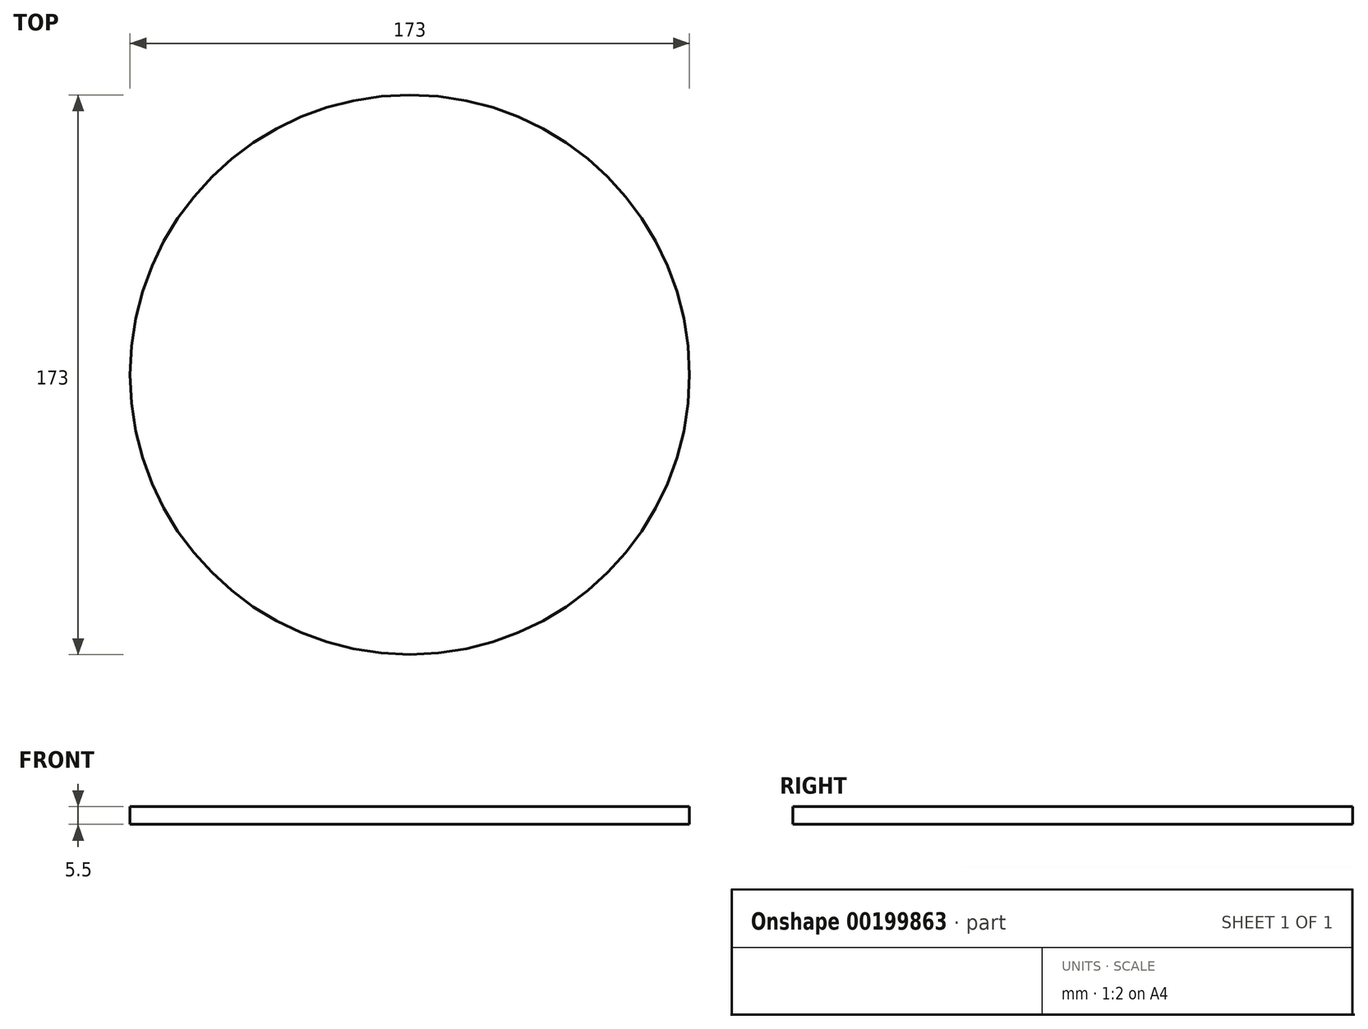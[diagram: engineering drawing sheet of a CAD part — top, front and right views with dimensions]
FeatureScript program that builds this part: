
annotation { "Feature Type Name" : "Feature", "Feature Type Description" : "" }
export const myFeature = defineFeature(function(context is Context, id is Id, definition is map)
    precondition{}
    {
        {
            var Q0;
            Q0=qCreatedBy(makeId("Top.planeOp"),FACE);
            var sketch = newSketch(context, id + "F0", { "sketchPlane" : qUnion([Q0])});
            skCircle(sketch, "E0", {"center": v(0, 0) * mm, "radius": 86.5 * mm});
            skLineSegment(sketch, "E1.bottom", {"start": v(29.9, 49.65) * mm, "end": v(-29.9, 49.65) * mm, "construction": true});
            skLineSegment(sketch, "E1.top", {"start": v(29.9, -49.65) * mm, "end": v(-29.9, -49.65) * mm, "construction": true});
            skLineSegment(sketch, "E1.left", {"start": v(29.9, 49.65) * mm, "end": v(29.9, -49.65) * mm, "construction": true});
            skLineSegment(sketch, "E1.right", {"start": v(-29.9, 49.65) * mm, "end": v(-29.9, -49.65) * mm, "construction": true});
            skCircle(sketch, "E2.cCircle", {"center": v(-29.9, 49.65) * mm, "radius": 2.9 * mm, "construction": true});
            skLineSegment(sketch, "E2.0", {"start": v(-31.57, 52.55) * mm, "end": v(-28.23, 52.55) * mm});
            skLineSegment(sketch, "E2.1", {"start": v(-28.23, 52.55) * mm, "end": v(-26.55, 49.65) * mm});
            skLineSegment(sketch, "E2.2", {"start": v(-26.55, 49.65) * mm, "end": v(-28.23, 46.75) * mm});
            skLineSegment(sketch, "E2.3", {"start": v(-28.23, 46.75) * mm, "end": v(-31.57, 46.75) * mm});
            skLineSegment(sketch, "E2.4", {"start": v(-31.57, 46.75) * mm, "end": v(-33.25, 49.65) * mm});
            skLineSegment(sketch, "E2.5", {"start": v(-33.25, 49.65) * mm, "end": v(-31.57, 52.55) * mm});
            skPoint(sketch, "E2.0.midPoint", {"position": v(-29.9, 52.55) * mm});
            skCircle(sketch, "E3.cCircle", {"center": v(29.9, 49.65) * mm, "radius": 2.9 * mm, "construction": true});
            skLineSegment(sketch, "E3.0", {"start": v(28.23, 52.55) * mm, "end": v(31.57, 52.55) * mm});
            skLineSegment(sketch, "E3.1", {"start": v(31.57, 52.55) * mm, "end": v(33.25, 49.65) * mm});
            skLineSegment(sketch, "E3.2", {"start": v(33.25, 49.65) * mm, "end": v(31.57, 46.75) * mm});
            skLineSegment(sketch, "E3.3", {"start": v(31.57, 46.75) * mm, "end": v(28.23, 46.75) * mm});
            skLineSegment(sketch, "E3.4", {"start": v(28.23, 46.75) * mm, "end": v(26.55, 49.65) * mm});
            skLineSegment(sketch, "E3.5", {"start": v(26.55, 49.65) * mm, "end": v(28.23, 52.55) * mm});
            skPoint(sketch, "E3.0.midPoint", {"position": v(29.9, 52.55) * mm});
            skCircle(sketch, "E4.cCircle", {"center": v(-29.9, -49.65) * mm, "radius": 2.9 * mm, "construction": true});
            skLineSegment(sketch, "E4.0", {"start": v(-28.23, -52.55) * mm, "end": v(-31.57, -52.55) * mm});
            skLineSegment(sketch, "E4.1", {"start": v(-31.57, -52.55) * mm, "end": v(-33.25, -49.65) * mm});
            skLineSegment(sketch, "E4.2", {"start": v(-33.25, -49.65) * mm, "end": v(-31.57, -46.75) * mm});
            skLineSegment(sketch, "E4.3", {"start": v(-31.57, -46.75) * mm, "end": v(-28.23, -46.75) * mm});
            skLineSegment(sketch, "E4.4", {"start": v(-28.23, -46.75) * mm, "end": v(-26.55, -49.65) * mm});
            skLineSegment(sketch, "E4.5", {"start": v(-26.55, -49.65) * mm, "end": v(-28.23, -52.55) * mm});
            skPoint(sketch, "E4.0.midPoint", {"position": v(-29.9, -52.55) * mm});
            skCircle(sketch, "E5.cCircle", {"center": v(29.9, -49.65) * mm, "radius": 2.9 * mm, "construction": true});
            skLineSegment(sketch, "E5.0", {"start": v(31.57, -52.55) * mm, "end": v(28.23, -52.55) * mm});
            skLineSegment(sketch, "E5.1", {"start": v(28.23, -52.55) * mm, "end": v(26.55, -49.65) * mm});
            skLineSegment(sketch, "E5.2", {"start": v(26.55, -49.65) * mm, "end": v(28.23, -46.75) * mm});
            skLineSegment(sketch, "E5.3", {"start": v(28.23, -46.75) * mm, "end": v(31.57, -46.75) * mm});
            skLineSegment(sketch, "E5.4", {"start": v(31.57, -46.75) * mm, "end": v(33.25, -49.65) * mm});
            skLineSegment(sketch, "E5.5", {"start": v(33.25, -49.65) * mm, "end": v(31.57, -52.55) * mm});
            skPoint(sketch, "E5.0.midPoint", {"position": v(29.9, -52.55) * mm});
            skLineSegment(sketch, "E6", {"start": v(0, 0) * mm, "end": v(125.93, 0) * mm, "construction": true});
            skCircle(sketch, "E7.0", {"center": v(0, 0) * mm, "radius": 85 * mm, "construction": true});
            skArc(sketch, "E8", {"start": v(84.99, 1.5) * mm, "mid": v(83.5, 0) * mm, "end": v(84.99, -1.5) * mm});
            skLineSegment(sketch, "E9.trimOffspring", {"start": v(84.97, 1.5) * mm, "end": v(86.49, 1.53) * mm});
            skLineSegment(sketch, "E10.trimOffspring", {"start": v(84.97, -1.5) * mm, "end": v(86.49, -1.53) * mm});
            skLineSegment(sketch, "E11.1.0", {"start": v(84.7, 6.89) * mm, "end": v(86.22, 7) * mm});
            skArc(sketch, "E11.1.1", {"start": v(84.72, 6.89) * mm, "mid": v(83.33, 5.3) * mm, "end": v(84.91, 3.9) * mm});
            skLineSegment(sketch, "E11.1.2", {"start": v(84.9, 3.9) * mm, "end": v(86.4, 3.96) * mm});
            skLineSegment(sketch, "E11.2.0", {"start": v(84.1, 12.24) * mm, "end": v(85.6, 12.46) * mm});
            skArc(sketch, "E11.2.1", {"start": v(84.11, 12.25) * mm, "mid": v(82.83, 10.57) * mm, "end": v(84.5, 9.27) * mm});
            skLineSegment(sketch, "E11.2.2", {"start": v(84.48, 9.27) * mm, "end": v(85.98, 9.43) * mm});
            skLineSegment(sketch, "E11.3.0", {"start": v(83.15, 17.55) * mm, "end": v(84.63, 17.87) * mm});
            skArc(sketch, "E11.3.1", {"start": v(83.17, 17.56) * mm, "mid": v(82, 15.8) * mm, "end": v(83.73, 14.61) * mm});
            skLineSegment(sketch, "E11.3.2", {"start": v(83.72, 14.6) * mm, "end": v(85.21, 14.87) * mm});
            skLineSegment(sketch, "E11.4.0", {"start": v(81.87, 22.8) * mm, "end": v(83.33, 23.2) * mm});
            skArc(sketch, "E11.4.1", {"start": v(81.89, 22.8) * mm, "mid": v(80.82, 20.97) * mm, "end": v(82.64, 19.9) * mm});
            skLineSegment(sketch, "E11.4.2", {"start": v(82.63, 19.89) * mm, "end": v(84.1, 20.24) * mm});
            skLineSegment(sketch, "E11.5.0", {"start": v(80.26, 27.94) * mm, "end": v(81.7, 28.44) * mm});
            skArc(sketch, "E11.5.1", {"start": v(80.28, 27.94) * mm, "mid": v(79.33, 26.05) * mm, "end": v(81.21, 25.1) * mm});
            skLineSegment(sketch, "E11.5.2", {"start": v(81.2, 25.09) * mm, "end": v(82.64, 25.54) * mm});
            skLineSegment(sketch, "E11.6.0", {"start": v(78.33, 32.97) * mm, "end": v(79.72, 33.56) * mm});
            skArc(sketch, "E11.6.1", {"start": v(78.34, 32.98) * mm, "mid": v(77.52, 31.03) * mm, "end": v(79.46, 30.2) * mm});
            skLineSegment(sketch, "E11.6.2", {"start": v(79.44, 30.19) * mm, "end": v(80.86, 30.73) * mm});
            skLineSegment(sketch, "E11.7.0", {"start": v(76.08, 37.88) * mm, "end": v(77.43, 38.55) * mm});
            skArc(sketch, "E11.7.1", {"start": v(76.1, 37.88) * mm, "mid": v(75.4, 35.89) * mm, "end": v(77.38, 35.17) * mm});
            skLineSegment(sketch, "E11.7.2", {"start": v(77.37, 35.17) * mm, "end": v(78.75, 35.8) * mm});
            skLineSegment(sketch, "E11.8.0", {"start": v(73.52, 42.62) * mm, "end": v(74.83, 43.38) * mm});
            skArc(sketch, "E11.8.1", {"start": v(73.54, 42.63) * mm, "mid": v(72.97, 40.6) * mm, "end": v(75, 40) * mm});
            skLineSegment(sketch, "E11.8.2", {"start": v(74.98, 40) * mm, "end": v(76.32, 40.72) * mm});
            skLineSegment(sketch, "E11.9.0", {"start": v(70.67, 47.2) * mm, "end": v(71.93, 48.04) * mm});
            skArc(sketch, "E11.9.1", {"start": v(70.68, 47.2) * mm, "mid": v(70.24, 45.14) * mm, "end": v(72.3, 44.69) * mm});
            skLineSegment(sketch, "E11.9.2", {"start": v(72.3, 44.68) * mm, "end": v(73.58, 45.47) * mm});
            skLineSegment(sketch, "E11.10.0", {"start": v(67.54, 51.59) * mm, "end": v(68.74, 52.5) * mm});
            skArc(sketch, "E11.10.1", {"start": v(67.55, 51.6) * mm, "mid": v(67.24, 49.5) * mm, "end": v(69.33, 49.18) * mm});
            skLineSegment(sketch, "E11.10.2", {"start": v(69.32, 49.17) * mm, "end": v(70.55, 50.05) * mm});
            skLineSegment(sketch, "E11.11.0", {"start": v(64.13, 55.77) * mm, "end": v(65.27, 56.76) * mm});
            skArc(sketch, "E11.11.1", {"start": v(64.14, 55.78) * mm, "mid": v(63.96, 53.67) * mm, "end": v(66.07, 53.48) * mm});
            skLineSegment(sketch, "E11.11.2", {"start": v(66.06, 53.47) * mm, "end": v(67.23, 54.42) * mm});
            skLineSegment(sketch, "E11.12.0", {"start": v(60.46, 59.72) * mm, "end": v(61.54, 60.79) * mm});
            skArc(sketch, "E11.12.1", {"start": v(60.47, 59.73) * mm, "mid": v(60.43, 57.62) * mm, "end": v(62.54, 57.56) * mm});
            skLineSegment(sketch, "E11.12.2", {"start": v(62.53, 57.55) * mm, "end": v(63.65, 58.58) * mm});
            skLineSegment(sketch, "E11.13.0", {"start": v(56.55, 63.44) * mm, "end": v(57.56, 64.57) * mm});
            skArc(sketch, "E11.13.1", {"start": v(56.56, 63.45) * mm, "mid": v(56.66, 61.34) * mm, "end": v(58.77, 61.41) * mm});
            skLineSegment(sketch, "E11.13.2", {"start": v(58.76, 61.4) * mm, "end": v(59.8, 62.5) * mm});
            skLineSegment(sketch, "E11.14.0", {"start": v(52.42, 66.9) * mm, "end": v(53.35, 68.09) * mm});
            skArc(sketch, "E11.14.1", {"start": v(52.42, 66.9) * mm, "mid": v(52.65, 64.8) * mm, "end": v(54.75, 65.02) * mm});
            skLineSegment(sketch, "E11.14.2", {"start": v(54.74, 65) * mm, "end": v(55.72, 66.16) * mm});
            skLineSegment(sketch, "E11.15.0", {"start": v(48.07, 70.09) * mm, "end": v(48.92, 71.34) * mm});
            skArc(sketch, "E11.15.1", {"start": v(48.08, 70.1) * mm, "mid": v(48.43, 68.02) * mm, "end": v(50.52, 68.36) * mm});
            skLineSegment(sketch, "E11.15.2", {"start": v(50.51, 68.35) * mm, "end": v(51.41, 69.56) * mm});
            skLineSegment(sketch, "E11.16.0", {"start": v(43.53, 73) * mm, "end": v(44.3, 74.3) * mm});
            skArc(sketch, "E11.16.1", {"start": v(43.53, 73) * mm, "mid": v(44.02, 70.95) * mm, "end": v(46.08, 71.42) * mm});
            skLineSegment(sketch, "E11.16.2", {"start": v(46.07, 71.41) * mm, "end": v(46.9, 72.69) * mm});
            skLineSegment(sketch, "E11.17.0", {"start": v(38.8, 75.6) * mm, "end": v(39.5, 76.95) * mm});
            skArc(sketch, "E11.17.1", {"start": v(38.81, 75.62) * mm, "mid": v(39.43, 73.6) * mm, "end": v(41.46, 74.2) * mm});
            skLineSegment(sketch, "E11.17.2", {"start": v(41.45, 74.2) * mm, "end": v(42.2, 75.51) * mm});
            skLineSegment(sketch, "E11.18.0", {"start": v(33.94, 77.92) * mm, "end": v(34.54, 79.3) * mm});
            skArc(sketch, "E11.18.1", {"start": v(33.94, 77.93) * mm, "mid": v(34.69, 75.95) * mm, "end": v(36.67, 76.68) * mm});
            skLineSegment(sketch, "E11.18.2", {"start": v(36.66, 76.67) * mm, "end": v(37.32, 78.04) * mm});
            skLineSegment(sketch, "E11.19.0", {"start": v(28.92, 79.91) * mm, "end": v(29.44, 81.34) * mm});
            skArc(sketch, "E11.19.1", {"start": v(28.93, 79.93) * mm, "mid": v(29.8, 78) * mm, "end": v(31.73, 78.85) * mm});
            skLineSegment(sketch, "E11.19.2", {"start": v(31.73, 78.84) * mm, "end": v(32.3, 80.25) * mm});
            skLineSegment(sketch, "E11.20.0", {"start": v(23.8, 81.59) * mm, "end": v(24.22, 83.04) * mm});
            skArc(sketch, "E11.20.1", {"start": v(23.8, 81.6) * mm, "mid": v(24.8, 79.73) * mm, "end": v(26.67, 80.7) * mm});
            skLineSegment(sketch, "E11.20.2", {"start": v(26.66, 80.7) * mm, "end": v(27.14, 82.13) * mm});
            skLineSegment(sketch, "E11.21.0", {"start": v(18.58, 82.93) * mm, "end": v(18.9, 84.4) * mm});
            skArc(sketch, "E11.21.1", {"start": v(18.58, 82.94) * mm, "mid": v(19.69, 81.15) * mm, "end": v(21.5, 82.24) * mm});
            skLineSegment(sketch, "E11.21.2", {"start": v(21.5, 82.22) * mm, "end": v(21.87, 83.69) * mm});
            skLineSegment(sketch, "E11.22.0", {"start": v(13.28, 83.94) * mm, "end": v(13.51, 85.44) * mm});
            skArc(sketch, "E11.22.1", {"start": v(13.28, 83.96) * mm, "mid": v(14.5, 82.23) * mm, "end": v(16.23, 83.44) * mm});
            skLineSegment(sketch, "E11.22.2", {"start": v(16.23, 83.42) * mm, "end": v(16.52, 84.9) * mm});
            skLineSegment(sketch, "E11.23.0", {"start": v(7.93, 84.62) * mm, "end": v(8.07, 86.12) * mm});
            skArc(sketch, "E11.23.1", {"start": v(7.93, 84.63) * mm, "mid": v(9.25, 82.99) * mm, "end": v(10.91, 84.3) * mm});
            skLineSegment(sketch, "E11.23.2", {"start": v(10.9, 84.28) * mm, "end": v(11.1, 85.78) * mm});
            skLineSegment(sketch, "E11.24.0", {"start": v(2.55, 84.95) * mm, "end": v(2.6, 86.46) * mm});
            skArc(sketch, "E11.24.1", {"start": v(2.55, 84.96) * mm, "mid": v(3.97, 83.4) * mm, "end": v(5.54, 84.82) * mm});
            skLineSegment(sketch, "E11.24.2", {"start": v(5.54, 84.8) * mm, "end": v(5.64, 86.32) * mm});
            skLineSegment(sketch, "E11.25.0", {"start": v(-2.85, 84.94) * mm, "end": v(-2.9, 86.45) * mm});
            skArc(sketch, "E11.25.1", {"start": v(-2.85, 84.95) * mm, "mid": v(-1.32, 83.49) * mm, "end": v(0.15, 85) * mm});
            skLineSegment(sketch, "E11.25.2", {"start": v(0.15, 84.99) * mm, "end": v(0.15, 86.5) * mm});
            skLineSegment(sketch, "E11.26.0", {"start": v(-8.23, 84.59) * mm, "end": v(-8.38, 86.1) * mm});
            skArc(sketch, "E11.26.1", {"start": v(-8.23, 84.6) * mm, "mid": v(-6.62, 83.24) * mm, "end": v(-5.24, 84.84) * mm});
            skLineSegment(sketch, "E11.26.2", {"start": v(-5.24, 84.83) * mm, "end": v(-5.33, 86.34) * mm});
            skLineSegment(sketch, "E11.27.0", {"start": v(-13.58, 83.9) * mm, "end": v(-13.82, 85.39) * mm});
            skArc(sketch, "E11.27.1", {"start": v(-13.58, 83.9) * mm, "mid": v(-11.88, 82.65) * mm, "end": v(-10.61, 84.34) * mm});
            skLineSegment(sketch, "E11.27.2", {"start": v(-10.6, 84.32) * mm, "end": v(-10.8, 85.82) * mm});
            skLineSegment(sketch, "E11.28.0", {"start": v(-18.87, 82.87) * mm, "end": v(-19.2, 84.34) * mm});
            skArc(sketch, "E11.28.1", {"start": v(-18.87, 82.88) * mm, "mid": v(-17.1, 81.73) * mm, "end": v(-15.94, 83.5) * mm});
            skLineSegment(sketch, "E11.28.2", {"start": v(-15.94, 83.48) * mm, "end": v(-16.22, 84.97) * mm});
            skLineSegment(sketch, "E11.29.0", {"start": v(-24.09, 81.5) * mm, "end": v(-24.52, 82.95) * mm});
            skArc(sketch, "E11.29.1", {"start": v(-24.1, 81.51) * mm, "mid": v(-22.25, 80.48) * mm, "end": v(-21.2, 82.31) * mm});
            skLineSegment(sketch, "E11.29.2", {"start": v(-21.2, 82.3) * mm, "end": v(-21.58, 83.77) * mm});
            skLineSegment(sketch, "E11.30.0", {"start": v(-29.2, 79.8) * mm, "end": v(-29.73, 81.23) * mm});
            skArc(sketch, "E11.30.1", {"start": v(-29.21, 79.82) * mm, "mid": v(-27.31, 78.9) * mm, "end": v(-26.38, 80.8) * mm});
            skLineSegment(sketch, "E11.30.2", {"start": v(-26.37, 80.8) * mm, "end": v(-26.84, 82.23) * mm});
            skLineSegment(sketch, "E11.31.0", {"start": v(-34.21, 77.8) * mm, "end": v(-34.82, 79.18) * mm});
            skArc(sketch, "E11.31.1", {"start": v(-34.22, 77.8) * mm, "mid": v(-32.26, 77.02) * mm, "end": v(-31.45, 78.97) * mm});
            skLineSegment(sketch, "E11.31.2", {"start": v(-31.45, 78.96) * mm, "end": v(-32, 80.36) * mm});
            skLineSegment(sketch, "E11.32.0", {"start": v(-39.08, 75.47) * mm, "end": v(-39.77, 76.81) * mm});
            skArc(sketch, "E11.32.1", {"start": v(-39.08, 75.48) * mm, "mid": v(-37.08, 74.82) * mm, "end": v(-36.4, 76.81) * mm});
            skLineSegment(sketch, "E11.32.2", {"start": v(-36.4, 76.8) * mm, "end": v(-37.04, 78.17) * mm});
            skLineSegment(sketch, "E11.33.0", {"start": v(-43.79, 72.84) * mm, "end": v(-44.57, 74.14) * mm});
            skArc(sketch, "E11.33.1", {"start": v(-43.8, 72.85) * mm, "mid": v(-41.75, 72.31) * mm, "end": v(-41.2, 74.35) * mm});
            skLineSegment(sketch, "E11.33.2", {"start": v(-41.19, 74.34) * mm, "end": v(-41.92, 75.66) * mm});
            skLineSegment(sketch, "E11.34.0", {"start": v(-48.32, 69.92) * mm, "end": v(-49.18, 71.16) * mm});
            skArc(sketch, "E11.34.1", {"start": v(-48.32, 69.93) * mm, "mid": v(-46.25, 69.52) * mm, "end": v(-45.83, 71.59) * mm});
            skLineSegment(sketch, "E11.34.2", {"start": v(-45.82, 71.58) * mm, "end": v(-46.64, 72.85) * mm});
            skLineSegment(sketch, "E11.35.0", {"start": v(-52.65, 66.71) * mm, "end": v(-53.6, 67.9) * mm});
            skArc(sketch, "E11.35.1", {"start": v(-52.66, 66.72) * mm, "mid": v(-50.57, 66.45) * mm, "end": v(-50.28, 68.54) * mm});
            skLineSegment(sketch, "E11.35.2", {"start": v(-50.27, 68.53) * mm, "end": v(-51.16, 69.75) * mm});
            skLineSegment(sketch, "E11.36.0", {"start": v(-56.78, 63.24) * mm, "end": v(-57.8, 64.36) * mm});
            skArc(sketch, "E11.36.1", {"start": v(-56.79, 63.25) * mm, "mid": v(-54.68, 63.1) * mm, "end": v(-54.52, 65.21) * mm});
            skLineSegment(sketch, "E11.36.2", {"start": v(-54.51, 65.2) * mm, "end": v(-55.48, 66.36) * mm});
            skLineSegment(sketch, "E11.37.0", {"start": v(-60.68, 59.5) * mm, "end": v(-61.76, 60.57) * mm});
            skArc(sketch, "E11.37.1", {"start": v(-60.69, 59.52) * mm, "mid": v(-58.57, 59.5) * mm, "end": v(-58.55, 61.62) * mm});
            skLineSegment(sketch, "E11.37.2", {"start": v(-58.54, 61.61) * mm, "end": v(-59.58, 62.7) * mm});
            skLineSegment(sketch, "E11.38.0", {"start": v(-64.33, 55.54) * mm, "end": v(-65.47, 56.53) * mm});
            skArc(sketch, "E11.38.1", {"start": v(-64.34, 55.55) * mm, "mid": v(-62.23, 55.68) * mm, "end": v(-62.34, 57.78) * mm});
            skLineSegment(sketch, "E11.38.2", {"start": v(-62.33, 57.78) * mm, "end": v(-63.44, 58.8) * mm});
            skLineSegment(sketch, "E11.39.0", {"start": v(-67.72, 51.35) * mm, "end": v(-68.93, 52.26) * mm});
            skArc(sketch, "E11.39.1", {"start": v(-67.73, 51.36) * mm, "mid": v(-65.64, 51.62) * mm, "end": v(-65.88, 53.71) * mm});
            skLineSegment(sketch, "E11.39.2", {"start": v(-65.87, 53.7) * mm, "end": v(-67.04, 54.66) * mm});
            skLineSegment(sketch, "E11.40.0", {"start": v(-70.84, 46.95) * mm, "end": v(-72.1, 47.79) * mm});
            skArc(sketch, "E11.40.1", {"start": v(-70.85, 46.96) * mm, "mid": v(-68.78, 47.35) * mm, "end": v(-69.15, 49.43) * mm});
            skLineSegment(sketch, "E11.40.2", {"start": v(-69.14, 49.42) * mm, "end": v(-70.37, 50.3) * mm});
            skLineSegment(sketch, "E11.41.0", {"start": v(-73.68, 42.36) * mm, "end": v(-74.99, 43.12) * mm});
            skArc(sketch, "E11.41.1", {"start": v(-73.69, 42.37) * mm, "mid": v(-71.64, 42.9) * mm, "end": v(-72.15, 44.94) * mm});
            skLineSegment(sketch, "E11.41.2", {"start": v(-72.14, 44.94) * mm, "end": v(-73.42, 45.74) * mm});
            skLineSegment(sketch, "E11.42.0", {"start": v(-76.21, 37.6) * mm, "end": v(-77.57, 38.27) * mm});
            skArc(sketch, "E11.42.1", {"start": v(-76.23, 37.6) * mm, "mid": v(-74.22, 38.26) * mm, "end": v(-74.85, 40.28) * mm});
            skLineSegment(sketch, "E11.42.2", {"start": v(-74.84, 40.27) * mm, "end": v(-76.17, 40.99) * mm});
            skLineSegment(sketch, "E11.43.0", {"start": v(-78.45, 32.7) * mm, "end": v(-79.84, 33.28) * mm});
            skArc(sketch, "E11.43.1", {"start": v(-78.46, 32.7) * mm, "mid": v(-76.5, 33.48) * mm, "end": v(-77.26, 35.45) * mm});
            skLineSegment(sketch, "E11.43.2", {"start": v(-77.24, 35.44) * mm, "end": v(-78.62, 36.07) * mm});
            skLineSegment(sketch, "E11.44.0", {"start": v(-80.36, 27.65) * mm, "end": v(-81.8, 28.15) * mm});
            skArc(sketch, "E11.44.1", {"start": v(-80.37, 27.66) * mm, "mid": v(-78.46, 28.56) * mm, "end": v(-79.35, 30.48) * mm});
            skLineSegment(sketch, "E11.44.2", {"start": v(-79.34, 30.47) * mm, "end": v(-80.75, 31.01) * mm});
            skLineSegment(sketch, "E11.45.0", {"start": v(-81.95, 22.5) * mm, "end": v(-83.41, 22.9) * mm});
            skArc(sketch, "E11.45.1", {"start": v(-81.97, 22.5) * mm, "mid": v(-80.12, 23.52) * mm, "end": v(-81.12, 25.38) * mm});
            skLineSegment(sketch, "E11.45.2", {"start": v(-81.1, 25.38) * mm, "end": v(-82.55, 25.83) * mm});
            skLineSegment(sketch, "E11.46.0", {"start": v(-83.22, 17.26) * mm, "end": v(-84.7, 17.56) * mm});
            skArc(sketch, "E11.46.1", {"start": v(-83.23, 17.26) * mm, "mid": v(-81.45, 18.4) * mm, "end": v(-82.57, 20.19) * mm});
            skLineSegment(sketch, "E11.46.2", {"start": v(-82.56, 20.18) * mm, "end": v(-84.03, 20.54) * mm});
            skLineSegment(sketch, "E11.47.0", {"start": v(-84.14, 11.95) * mm, "end": v(-85.64, 12.16) * mm});
            skArc(sketch, "E11.47.1", {"start": v(-84.16, 11.95) * mm, "mid": v(-82.45, 13.2) * mm, "end": v(-83.68, 14.9) * mm});
            skLineSegment(sketch, "E11.47.2", {"start": v(-83.67, 14.9) * mm, "end": v(-85.16, 15.17) * mm});
            skLineSegment(sketch, "E11.48.0", {"start": v(-84.73, 6.58) * mm, "end": v(-86.24, 6.7) * mm});
            skArc(sketch, "E11.48.1", {"start": v(-84.74, 6.59) * mm, "mid": v(-83.12, 7.94) * mm, "end": v(-84.46, 9.57) * mm});
            skLineSegment(sketch, "E11.48.2", {"start": v(-84.45, 9.57) * mm, "end": v(-85.95, 9.74) * mm});
            skLineSegment(sketch, "E11.49.0", {"start": v(-84.98, 1.2) * mm, "end": v(-86.5, 1.22) * mm});
            skArc(sketch, "E11.49.1", {"start": v(-85, 1.2) * mm, "mid": v(-83.46, 2.65) * mm, "end": v(-84.9, 4.2) * mm});
            skLineSegment(sketch, "E11.49.2", {"start": v(-84.88, 4.2) * mm, "end": v(-86.4, 4.27) * mm});
            skLineSegment(sketch, "E11.50.0", {"start": v(-84.88, -4.2) * mm, "end": v(-86.4, -4.27) * mm});
            skArc(sketch, "E11.50.1", {"start": v(-84.9, -4.2) * mm, "mid": v(-83.46, -2.65) * mm, "end": v(-85, -1.2) * mm});
            skLineSegment(sketch, "E11.50.2", {"start": v(-84.98, -1.2) * mm, "end": v(-86.5, -1.22) * mm});
            skLineSegment(sketch, "E11.51.0", {"start": v(-84.45, -9.57) * mm, "end": v(-85.95, -9.74) * mm});
            skArc(sketch, "E11.51.1", {"start": v(-84.46, -9.57) * mm, "mid": v(-83.12, -7.94) * mm, "end": v(-84.74, -6.59) * mm});
            skLineSegment(sketch, "E11.51.2", {"start": v(-84.73, -6.58) * mm, "end": v(-86.24, -6.7) * mm});
            skLineSegment(sketch, "E11.52.0", {"start": v(-83.67, -14.9) * mm, "end": v(-85.16, -15.17) * mm});
            skArc(sketch, "E11.52.1", {"start": v(-83.68, -14.9) * mm, "mid": v(-82.45, -13.2) * mm, "end": v(-84.16, -11.95) * mm});
            skLineSegment(sketch, "E11.52.2", {"start": v(-84.14, -11.95) * mm, "end": v(-85.64, -12.16) * mm});
            skLineSegment(sketch, "E11.53.0", {"start": v(-82.56, -20.18) * mm, "end": v(-84.03, -20.54) * mm});
            skArc(sketch, "E11.53.1", {"start": v(-82.57, -20.19) * mm, "mid": v(-81.45, -18.4) * mm, "end": v(-83.23, -17.26) * mm});
            skLineSegment(sketch, "E11.53.2", {"start": v(-83.22, -17.26) * mm, "end": v(-84.7, -17.56) * mm});
            skLineSegment(sketch, "E11.54.0", {"start": v(-81.1, -25.38) * mm, "end": v(-82.55, -25.83) * mm});
            skArc(sketch, "E11.54.1", {"start": v(-81.12, -25.38) * mm, "mid": v(-80.12, -23.52) * mm, "end": v(-81.97, -22.5) * mm});
            skLineSegment(sketch, "E11.54.2", {"start": v(-81.95, -22.5) * mm, "end": v(-83.41, -22.9) * mm});
            skLineSegment(sketch, "E11.55.0", {"start": v(-79.34, -30.47) * mm, "end": v(-80.75, -31.01) * mm});
            skArc(sketch, "E11.55.1", {"start": v(-79.35, -30.48) * mm, "mid": v(-78.46, -28.56) * mm, "end": v(-80.37, -27.66) * mm});
            skLineSegment(sketch, "E11.55.2", {"start": v(-80.36, -27.65) * mm, "end": v(-81.8, -28.15) * mm});
            skLineSegment(sketch, "E11.56.0", {"start": v(-77.24, -35.44) * mm, "end": v(-78.62, -36.07) * mm});
            skArc(sketch, "E11.56.1", {"start": v(-77.26, -35.45) * mm, "mid": v(-76.5, -33.48) * mm, "end": v(-78.46, -32.7) * mm});
            skLineSegment(sketch, "E11.56.2", {"start": v(-78.45, -32.7) * mm, "end": v(-79.84, -33.28) * mm});
            skLineSegment(sketch, "E11.57.0", {"start": v(-74.84, -40.27) * mm, "end": v(-76.17, -40.99) * mm});
            skArc(sketch, "E11.57.1", {"start": v(-74.85, -40.28) * mm, "mid": v(-74.22, -38.26) * mm, "end": v(-76.23, -37.6) * mm});
            skLineSegment(sketch, "E11.57.2", {"start": v(-76.21, -37.6) * mm, "end": v(-77.57, -38.27) * mm});
            skLineSegment(sketch, "E11.58.0", {"start": v(-72.14, -44.94) * mm, "end": v(-73.42, -45.74) * mm});
            skArc(sketch, "E11.58.1", {"start": v(-72.15, -44.94) * mm, "mid": v(-71.64, -42.9) * mm, "end": v(-73.69, -42.37) * mm});
            skLineSegment(sketch, "E11.58.2", {"start": v(-73.68, -42.36) * mm, "end": v(-74.99, -43.12) * mm});
            skLineSegment(sketch, "E11.59.0", {"start": v(-69.14, -49.42) * mm, "end": v(-70.37, -50.3) * mm});
            skArc(sketch, "E11.59.1", {"start": v(-69.15, -49.43) * mm, "mid": v(-68.78, -47.35) * mm, "end": v(-70.85, -46.96) * mm});
            skLineSegment(sketch, "E11.59.2", {"start": v(-70.84, -46.95) * mm, "end": v(-72.1, -47.79) * mm});
            skLineSegment(sketch, "E11.60.0", {"start": v(-65.87, -53.7) * mm, "end": v(-67.04, -54.66) * mm});
            skArc(sketch, "E11.60.1", {"start": v(-65.88, -53.71) * mm, "mid": v(-65.64, -51.62) * mm, "end": v(-67.73, -51.36) * mm});
            skLineSegment(sketch, "E11.60.2", {"start": v(-67.72, -51.35) * mm, "end": v(-68.93, -52.26) * mm});
            skLineSegment(sketch, "E11.61.0", {"start": v(-62.33, -57.78) * mm, "end": v(-63.44, -58.8) * mm});
            skArc(sketch, "E11.61.1", {"start": v(-62.34, -57.78) * mm, "mid": v(-62.23, -55.68) * mm, "end": v(-64.34, -55.55) * mm});
            skLineSegment(sketch, "E11.61.2", {"start": v(-64.33, -55.54) * mm, "end": v(-65.47, -56.53) * mm});
            skLineSegment(sketch, "E11.62.0", {"start": v(-58.54, -61.61) * mm, "end": v(-59.58, -62.7) * mm});
            skArc(sketch, "E11.62.1", {"start": v(-58.55, -61.62) * mm, "mid": v(-58.57, -59.5) * mm, "end": v(-60.69, -59.52) * mm});
            skLineSegment(sketch, "E11.62.2", {"start": v(-60.68, -59.5) * mm, "end": v(-61.76, -60.57) * mm});
            skLineSegment(sketch, "E11.63.0", {"start": v(-54.51, -65.2) * mm, "end": v(-55.48, -66.36) * mm});
            skArc(sketch, "E11.63.1", {"start": v(-54.52, -65.21) * mm, "mid": v(-54.68, -63.1) * mm, "end": v(-56.79, -63.25) * mm});
            skLineSegment(sketch, "E11.63.2", {"start": v(-56.78, -63.24) * mm, "end": v(-57.8, -64.36) * mm});
            skLineSegment(sketch, "E11.64.0", {"start": v(-50.27, -68.53) * mm, "end": v(-51.16, -69.75) * mm});
            skArc(sketch, "E11.64.1", {"start": v(-50.28, -68.54) * mm, "mid": v(-50.57, -66.45) * mm, "end": v(-52.66, -66.72) * mm});
            skLineSegment(sketch, "E11.64.2", {"start": v(-52.65, -66.71) * mm, "end": v(-53.6, -67.9) * mm});
            skLineSegment(sketch, "E11.65.0", {"start": v(-45.82, -71.58) * mm, "end": v(-46.64, -72.85) * mm});
            skArc(sketch, "E11.65.1", {"start": v(-45.83, -71.59) * mm, "mid": v(-46.25, -69.52) * mm, "end": v(-48.32, -69.93) * mm});
            skLineSegment(sketch, "E11.65.2", {"start": v(-48.32, -69.92) * mm, "end": v(-49.18, -71.16) * mm});
            skLineSegment(sketch, "E11.66.0", {"start": v(-41.19, -74.34) * mm, "end": v(-41.92, -75.66) * mm});
            skArc(sketch, "E11.66.1", {"start": v(-41.2, -74.35) * mm, "mid": v(-41.75, -72.31) * mm, "end": v(-43.8, -72.85) * mm});
            skLineSegment(sketch, "E11.66.2", {"start": v(-43.79, -72.84) * mm, "end": v(-44.57, -74.14) * mm});
            skLineSegment(sketch, "E11.67.0", {"start": v(-36.4, -76.8) * mm, "end": v(-37.04, -78.17) * mm});
            skArc(sketch, "E11.67.1", {"start": v(-36.4, -76.81) * mm, "mid": v(-37.08, -74.82) * mm, "end": v(-39.08, -75.48) * mm});
            skLineSegment(sketch, "E11.67.2", {"start": v(-39.08, -75.47) * mm, "end": v(-39.77, -76.81) * mm});
            skLineSegment(sketch, "E11.68.0", {"start": v(-31.45, -78.96) * mm, "end": v(-32, -80.36) * mm});
            skArc(sketch, "E11.68.1", {"start": v(-31.45, -78.97) * mm, "mid": v(-32.26, -77.02) * mm, "end": v(-34.22, -77.8) * mm});
            skLineSegment(sketch, "E11.68.2", {"start": v(-34.21, -77.8) * mm, "end": v(-34.82, -79.18) * mm});
            skLineSegment(sketch, "E11.69.0", {"start": v(-26.37, -80.8) * mm, "end": v(-26.84, -82.23) * mm});
            skArc(sketch, "E11.69.1", {"start": v(-26.38, -80.8) * mm, "mid": v(-27.31, -78.9) * mm, "end": v(-29.21, -79.82) * mm});
            skLineSegment(sketch, "E11.69.2", {"start": v(-29.2, -79.8) * mm, "end": v(-29.73, -81.23) * mm});
            skLineSegment(sketch, "E11.70.0", {"start": v(-21.2, -82.3) * mm, "end": v(-21.58, -83.77) * mm});
            skArc(sketch, "E11.70.1", {"start": v(-21.2, -82.31) * mm, "mid": v(-22.25, -80.48) * mm, "end": v(-24.1, -81.51) * mm});
            skLineSegment(sketch, "E11.70.2", {"start": v(-24.09, -81.5) * mm, "end": v(-24.52, -82.95) * mm});
            skLineSegment(sketch, "E11.71.0", {"start": v(-15.94, -83.48) * mm, "end": v(-16.22, -84.97) * mm});
            skArc(sketch, "E11.71.1", {"start": v(-15.94, -83.5) * mm, "mid": v(-17.1, -81.73) * mm, "end": v(-18.87, -82.88) * mm});
            skLineSegment(sketch, "E11.71.2", {"start": v(-18.87, -82.87) * mm, "end": v(-19.2, -84.34) * mm});
            skLineSegment(sketch, "E11.72.0", {"start": v(-10.6, -84.32) * mm, "end": v(-10.8, -85.82) * mm});
            skArc(sketch, "E11.72.1", {"start": v(-10.61, -84.34) * mm, "mid": v(-11.88, -82.65) * mm, "end": v(-13.58, -83.9) * mm});
            skLineSegment(sketch, "E11.72.2", {"start": v(-13.58, -83.9) * mm, "end": v(-13.82, -85.39) * mm});
            skLineSegment(sketch, "E11.73.0", {"start": v(-5.24, -84.83) * mm, "end": v(-5.33, -86.34) * mm});
            skArc(sketch, "E11.73.1", {"start": v(-5.24, -84.84) * mm, "mid": v(-6.62, -83.24) * mm, "end": v(-8.23, -84.6) * mm});
            skLineSegment(sketch, "E11.73.2", {"start": v(-8.23, -84.59) * mm, "end": v(-8.38, -86.1) * mm});
            skLineSegment(sketch, "E11.74.0", {"start": v(0.15, -84.99) * mm, "end": v(0.15, -86.5) * mm});
            skArc(sketch, "E11.74.1", {"start": v(0.15, -85) * mm, "mid": v(-1.32, -83.49) * mm, "end": v(-2.85, -84.95) * mm});
            skLineSegment(sketch, "E11.74.2", {"start": v(-2.85, -84.94) * mm, "end": v(-2.9, -86.45) * mm});
            skLineSegment(sketch, "E11.75.0", {"start": v(5.54, -84.8) * mm, "end": v(5.64, -86.32) * mm});
            skArc(sketch, "E11.75.1", {"start": v(5.54, -84.82) * mm, "mid": v(3.97, -83.4) * mm, "end": v(2.55, -84.96) * mm});
            skLineSegment(sketch, "E11.75.2", {"start": v(2.55, -84.95) * mm, "end": v(2.6, -86.46) * mm});
            skLineSegment(sketch, "E11.76.0", {"start": v(10.9, -84.28) * mm, "end": v(11.1, -85.78) * mm});
            skArc(sketch, "E11.76.1", {"start": v(10.91, -84.3) * mm, "mid": v(9.25, -82.99) * mm, "end": v(7.93, -84.63) * mm});
            skLineSegment(sketch, "E11.76.2", {"start": v(7.93, -84.62) * mm, "end": v(8.07, -86.12) * mm});
            skLineSegment(sketch, "E11.77.0", {"start": v(16.23, -83.42) * mm, "end": v(16.52, -84.9) * mm});
            skArc(sketch, "E11.77.1", {"start": v(16.23, -83.44) * mm, "mid": v(14.5, -82.23) * mm, "end": v(13.28, -83.96) * mm});
            skLineSegment(sketch, "E11.77.2", {"start": v(13.28, -83.94) * mm, "end": v(13.51, -85.44) * mm});
            skLineSegment(sketch, "E11.78.0", {"start": v(21.5, -82.22) * mm, "end": v(21.87, -83.69) * mm});
            skArc(sketch, "E11.78.1", {"start": v(21.5, -82.24) * mm, "mid": v(19.69, -81.15) * mm, "end": v(18.58, -82.94) * mm});
            skLineSegment(sketch, "E11.78.2", {"start": v(18.58, -82.93) * mm, "end": v(18.9, -84.4) * mm});
            skLineSegment(sketch, "E11.79.0", {"start": v(26.66, -80.7) * mm, "end": v(27.14, -82.13) * mm});
            skArc(sketch, "E11.79.1", {"start": v(26.67, -80.7) * mm, "mid": v(24.8, -79.73) * mm, "end": v(23.8, -81.6) * mm});
            skLineSegment(sketch, "E11.79.2", {"start": v(23.8, -81.59) * mm, "end": v(24.22, -83.04) * mm});
            skLineSegment(sketch, "E11.80.0", {"start": v(31.73, -78.84) * mm, "end": v(32.3, -80.25) * mm});
            skArc(sketch, "E11.80.1", {"start": v(31.73, -78.85) * mm, "mid": v(29.8, -78) * mm, "end": v(28.93, -79.93) * mm});
            skLineSegment(sketch, "E11.80.2", {"start": v(28.92, -79.91) * mm, "end": v(29.44, -81.34) * mm});
            skLineSegment(sketch, "E11.81.0", {"start": v(36.66, -76.67) * mm, "end": v(37.32, -78.04) * mm});
            skArc(sketch, "E11.81.1", {"start": v(36.67, -76.68) * mm, "mid": v(34.69, -75.95) * mm, "end": v(33.94, -77.93) * mm});
            skLineSegment(sketch, "E11.81.2", {"start": v(33.94, -77.92) * mm, "end": v(34.54, -79.3) * mm});
            skLineSegment(sketch, "E11.82.0", {"start": v(41.45, -74.2) * mm, "end": v(42.2, -75.51) * mm});
            skArc(sketch, "E11.82.1", {"start": v(41.46, -74.2) * mm, "mid": v(39.43, -73.6) * mm, "end": v(38.81, -75.62) * mm});
            skLineSegment(sketch, "E11.82.2", {"start": v(38.8, -75.6) * mm, "end": v(39.5, -76.95) * mm});
            skLineSegment(sketch, "E11.83.0", {"start": v(46.07, -71.41) * mm, "end": v(46.9, -72.69) * mm});
            skArc(sketch, "E11.83.1", {"start": v(46.08, -71.42) * mm, "mid": v(44.02, -70.95) * mm, "end": v(43.53, -73) * mm});
            skLineSegment(sketch, "E11.83.2", {"start": v(43.53, -73) * mm, "end": v(44.3, -74.3) * mm});
            skLineSegment(sketch, "E11.84.0", {"start": v(50.51, -68.35) * mm, "end": v(51.41, -69.56) * mm});
            skArc(sketch, "E11.84.1", {"start": v(50.52, -68.36) * mm, "mid": v(48.43, -68.02) * mm, "end": v(48.08, -70.1) * mm});
            skLineSegment(sketch, "E11.84.2", {"start": v(48.07, -70.09) * mm, "end": v(48.92, -71.34) * mm});
            skLineSegment(sketch, "E11.85.0", {"start": v(54.74, -65) * mm, "end": v(55.72, -66.16) * mm});
            skArc(sketch, "E11.85.1", {"start": v(54.75, -65.02) * mm, "mid": v(52.65, -64.8) * mm, "end": v(52.42, -66.9) * mm});
            skLineSegment(sketch, "E11.85.2", {"start": v(52.42, -66.9) * mm, "end": v(53.35, -68.09) * mm});
            skLineSegment(sketch, "E11.86.0", {"start": v(58.76, -61.4) * mm, "end": v(59.8, -62.5) * mm});
            skArc(sketch, "E11.86.1", {"start": v(58.77, -61.41) * mm, "mid": v(56.66, -61.34) * mm, "end": v(56.56, -63.45) * mm});
            skLineSegment(sketch, "E11.86.2", {"start": v(56.55, -63.44) * mm, "end": v(57.56, -64.57) * mm});
            skLineSegment(sketch, "E11.87.0", {"start": v(62.53, -57.55) * mm, "end": v(63.65, -58.58) * mm});
            skArc(sketch, "E11.87.1", {"start": v(62.54, -57.56) * mm, "mid": v(60.43, -57.62) * mm, "end": v(60.47, -59.73) * mm});
            skLineSegment(sketch, "E11.87.2", {"start": v(60.46, -59.72) * mm, "end": v(61.54, -60.79) * mm});
            skLineSegment(sketch, "E11.88.0", {"start": v(66.06, -53.47) * mm, "end": v(67.23, -54.42) * mm});
            skArc(sketch, "E11.88.1", {"start": v(66.07, -53.48) * mm, "mid": v(63.96, -53.67) * mm, "end": v(64.14, -55.78) * mm});
            skLineSegment(sketch, "E11.88.2", {"start": v(64.13, -55.77) * mm, "end": v(65.27, -56.76) * mm});
            skLineSegment(sketch, "E11.89.0", {"start": v(69.32, -49.17) * mm, "end": v(70.55, -50.05) * mm});
            skArc(sketch, "E11.89.1", {"start": v(69.33, -49.18) * mm, "mid": v(67.24, -49.5) * mm, "end": v(67.55, -51.6) * mm});
            skLineSegment(sketch, "E11.89.2", {"start": v(67.54, -51.59) * mm, "end": v(68.74, -52.5) * mm});
            skLineSegment(sketch, "E11.90.0", {"start": v(72.3, -44.68) * mm, "end": v(73.58, -45.47) * mm});
            skArc(sketch, "E11.90.1", {"start": v(72.3, -44.69) * mm, "mid": v(70.24, -45.14) * mm, "end": v(70.68, -47.2) * mm});
            skLineSegment(sketch, "E11.90.2", {"start": v(70.67, -47.2) * mm, "end": v(71.93, -48.04) * mm});
            skLineSegment(sketch, "E11.91.0", {"start": v(74.98, -40) * mm, "end": v(76.32, -40.72) * mm});
            skArc(sketch, "E11.91.1", {"start": v(75, -40) * mm, "mid": v(72.97, -40.6) * mm, "end": v(73.54, -42.63) * mm});
            skLineSegment(sketch, "E11.91.2", {"start": v(73.52, -42.62) * mm, "end": v(74.83, -43.38) * mm});
            skLineSegment(sketch, "E11.92.0", {"start": v(77.37, -35.17) * mm, "end": v(78.75, -35.8) * mm});
            skArc(sketch, "E11.92.1", {"start": v(77.38, -35.17) * mm, "mid": v(75.4, -35.89) * mm, "end": v(76.1, -37.88) * mm});
            skLineSegment(sketch, "E11.92.2", {"start": v(76.08, -37.88) * mm, "end": v(77.43, -38.55) * mm});
            skLineSegment(sketch, "E11.93.0", {"start": v(79.44, -30.19) * mm, "end": v(80.86, -30.73) * mm});
            skArc(sketch, "E11.93.1", {"start": v(79.46, -30.2) * mm, "mid": v(77.52, -31.03) * mm, "end": v(78.34, -32.98) * mm});
            skLineSegment(sketch, "E11.93.2", {"start": v(78.33, -32.97) * mm, "end": v(79.72, -33.56) * mm});
            skLineSegment(sketch, "E11.94.0", {"start": v(81.2, -25.09) * mm, "end": v(82.64, -25.54) * mm});
            skArc(sketch, "E11.94.1", {"start": v(81.21, -25.1) * mm, "mid": v(79.33, -26.05) * mm, "end": v(80.28, -27.94) * mm});
            skLineSegment(sketch, "E11.94.2", {"start": v(80.26, -27.94) * mm, "end": v(81.7, -28.44) * mm});
            skLineSegment(sketch, "E11.95.0", {"start": v(82.63, -19.89) * mm, "end": v(84.1, -20.24) * mm});
            skArc(sketch, "E11.95.1", {"start": v(82.64, -19.9) * mm, "mid": v(80.82, -20.97) * mm, "end": v(81.89, -22.8) * mm});
            skLineSegment(sketch, "E11.95.2", {"start": v(81.87, -22.8) * mm, "end": v(83.33, -23.2) * mm});
            skLineSegment(sketch, "E11.96.0", {"start": v(83.72, -14.6) * mm, "end": v(85.21, -14.87) * mm});
            skArc(sketch, "E11.96.1", {"start": v(83.73, -14.61) * mm, "mid": v(82, -15.8) * mm, "end": v(83.17, -17.56) * mm});
            skLineSegment(sketch, "E11.96.2", {"start": v(83.15, -17.55) * mm, "end": v(84.63, -17.87) * mm});
            skLineSegment(sketch, "E11.97.0", {"start": v(84.48, -9.27) * mm, "end": v(85.98, -9.43) * mm});
            skArc(sketch, "E11.97.1", {"start": v(84.5, -9.27) * mm, "mid": v(82.83, -10.57) * mm, "end": v(84.11, -12.25) * mm});
            skLineSegment(sketch, "E11.97.2", {"start": v(84.1, -12.24) * mm, "end": v(85.6, -12.46) * mm});
            skLineSegment(sketch, "E11.98.0", {"start": v(84.9, -3.9) * mm, "end": v(86.4, -3.96) * mm});
            skArc(sketch, "E11.98.1", {"start": v(84.91, -3.9) * mm, "mid": v(83.33, -5.3) * mm, "end": v(84.72, -6.89) * mm});
            skLineSegment(sketch, "E11.98.2", {"start": v(84.7, -6.89) * mm, "end": v(86.22, -7) * mm});
            skSolve(sketch);
        }
        {
            var Q0;
            {var subQ0=sQuery(id+"F0.wireOp",EDGE,"E11.32.0");Q0=makeQuery(id+"F0.imprint","IMPRINT",FACE,{"disambiguationData":[TD([[makeQuery(id+"F0.imprint","IMPRINT",EDGE,{"derivedFrom":subQ0}),-1.0]])]});}
            var Q1;
            {var subQ0=sQuery(id+"F0.wireOp",EDGE,"E11.96.0");Q1=makeQuery(id+"F0.imprint","IMPRINT",FACE,{"disambiguationData":[TD([[makeQuery(id+"F0.imprint","IMPRINT",EDGE,{"derivedFrom":subQ0}),-1.0]])]});}
            var Q2;
            {var subQ0=sQuery(id+"F0.wireOp",EDGE,"E11.80.0");Q2=makeQuery(id+"F0.imprint","IMPRINT",FACE,{"disambiguationData":[TD([[makeQuery(id+"F0.imprint","IMPRINT",EDGE,{"derivedFrom":subQ0}),-1.0]])]});}
            var Q3;
            {var subQ0=sQuery(id+"F0.wireOp",EDGE,"E11.64.0");Q3=makeQuery(id+"F0.imprint","IMPRINT",FACE,{"disambiguationData":[TD([[makeQuery(id+"F0.imprint","IMPRINT",EDGE,{"derivedFrom":subQ0}),-1.0]])]});}
            var Q4;
            {var subQ0=sQuery(id+"F0.wireOp",EDGE,"E11.48.0");Q4=makeQuery(id+"F0.imprint","IMPRINT",FACE,{"disambiguationData":[TD([[makeQuery(id+"F0.imprint","IMPRINT",EDGE,{"derivedFrom":subQ0}),-1.0]])]});}
            var Q5;
            {var subQ0=sQuery(id+"F0.wireOp",EDGE,"E11.78.0");Q5=makeQuery(id+"F0.imprint","IMPRINT",FACE,{"disambiguationData":[TD([[makeQuery(id+"F0.imprint","IMPRINT",EDGE,{"derivedFrom":subQ0}),-1.0]])]});}
            var Q6;
            {var subQ0=sQuery(id+"F0.wireOp",EDGE,"E11.46.0");Q6=makeQuery(id+"F0.imprint","IMPRINT",FACE,{"disambiguationData":[TD([[makeQuery(id+"F0.imprint","IMPRINT",EDGE,{"derivedFrom":subQ0}),-1.0]])]});}
            var Q7;
            {var subQ0=sQuery(id+"F0.wireOp",EDGE,"E11.30.0");Q7=makeQuery(id+"F0.imprint","IMPRINT",FACE,{"disambiguationData":[TD([[makeQuery(id+"F0.imprint","IMPRINT",EDGE,{"derivedFrom":subQ0}),-1.0]])]});}
            var Q8;
            {var subQ0=sQuery(id+"F0.wireOp",EDGE,"E11.94.0");Q8=makeQuery(id+"F0.imprint","IMPRINT",FACE,{"disambiguationData":[TD([[makeQuery(id+"F0.imprint","IMPRINT",EDGE,{"derivedFrom":subQ0}),-1.0]])]});}
            var Q9;
            {var subQ0=sQuery(id+"F0.wireOp",EDGE,"E11.79.0");Q9=makeQuery(id+"F0.imprint","IMPRINT",FACE,{"disambiguationData":[TD([[makeQuery(id+"F0.imprint","IMPRINT",EDGE,{"derivedFrom":subQ0}),-1.0]])]});}
            var Q10;
            {var subQ0=sQuery(id+"F0.wireOp",EDGE,"E11.63.0");Q10=makeQuery(id+"F0.imprint","IMPRINT",FACE,{"disambiguationData":[TD([[makeQuery(id+"F0.imprint","IMPRINT",EDGE,{"derivedFrom":subQ0}),-1.0]])]});}
            var Q11;
            {var subQ0=sQuery(id+"F0.wireOp",EDGE,"E11.47.0");Q11=makeQuery(id+"F0.imprint","IMPRINT",FACE,{"disambiguationData":[TD([[makeQuery(id+"F0.imprint","IMPRINT",EDGE,{"derivedFrom":subQ0}),-1.0]])]});}
            var Q12;
            {var subQ0=sQuery(id+"F0.wireOp",EDGE,"E11.31.0");Q12=makeQuery(id+"F0.imprint","IMPRINT",FACE,{"disambiguationData":[TD([[makeQuery(id+"F0.imprint","IMPRINT",EDGE,{"derivedFrom":subQ0}),-1.0]])]});}
            var Q13;
            {var subQ0=sQuery(id+"F0.wireOp",EDGE,"E11.95.0");Q13=makeQuery(id+"F0.imprint","IMPRINT",FACE,{"disambiguationData":[TD([[makeQuery(id+"F0.imprint","IMPRINT",EDGE,{"derivedFrom":subQ0}),-1.0]])]});}
            var Q14;
            {var subQ0=sQuery(id+"F0.wireOp",EDGE,"E11.17.0");Q14=makeQuery(id+"F0.imprint","IMPRINT",FACE,{"disambiguationData":[TD([[makeQuery(id+"F0.imprint","IMPRINT",EDGE,{"derivedFrom":subQ0}),-1.0]])]});}
            var Q15;
            {var subQ0=sQuery(id+"F0.wireOp",EDGE,"E11.81.0");Q15=makeQuery(id+"F0.imprint","IMPRINT",FACE,{"disambiguationData":[TD([[makeQuery(id+"F0.imprint","IMPRINT",EDGE,{"derivedFrom":subQ0}),-1.0]])]});}
            var Q16;
            {var subQ0=sQuery(id+"F0.wireOp",EDGE,"E11.65.0");Q16=makeQuery(id+"F0.imprint","IMPRINT",FACE,{"disambiguationData":[TD([[makeQuery(id+"F0.imprint","IMPRINT",EDGE,{"derivedFrom":subQ0}),-1.0]])]});}
            var Q17;
            {var subQ0=sQuery(id+"F0.wireOp",EDGE,"E11.49.0");Q17=makeQuery(id+"F0.imprint","IMPRINT",FACE,{"disambiguationData":[TD([[makeQuery(id+"F0.imprint","IMPRINT",EDGE,{"derivedFrom":subQ0}),-1.0]])]});}
            var Q18;
            {var subQ0=sQuery(id+"F0.wireOp",EDGE,"E11.33.0");Q18=makeQuery(id+"F0.imprint","IMPRINT",FACE,{"disambiguationData":[TD([[makeQuery(id+"F0.imprint","IMPRINT",EDGE,{"derivedFrom":subQ0}),-1.0]])]});}
            var Q19;
            {var subQ0=sQuery(id+"F0.wireOp",EDGE,"E11.97.0");Q19=makeQuery(id+"F0.imprint","IMPRINT",FACE,{"disambiguationData":[TD([[makeQuery(id+"F0.imprint","IMPRINT",EDGE,{"derivedFrom":subQ0}),-1.0]])]});}
            var Q20;
            {var subQ0=sQuery(id+"F0.wireOp",EDGE,"E11.18.0");Q20=makeQuery(id+"F0.imprint","IMPRINT",FACE,{"disambiguationData":[TD([[makeQuery(id+"F0.imprint","IMPRINT",EDGE,{"derivedFrom":subQ0}),-1.0]])]});}
            var Q21;
            {var subQ0=sQuery(id+"F0.wireOp",EDGE,"E11.82.0");Q21=makeQuery(id+"F0.imprint","IMPRINT",FACE,{"disambiguationData":[TD([[makeQuery(id+"F0.imprint","IMPRINT",EDGE,{"derivedFrom":subQ0}),-1.0]])]});}
            var Q22;
            {var subQ0=sQuery(id+"F0.wireOp",EDGE,"E11.66.0");Q22=makeQuery(id+"F0.imprint","IMPRINT",FACE,{"disambiguationData":[TD([[makeQuery(id+"F0.imprint","IMPRINT",EDGE,{"derivedFrom":subQ0}),-1.0]])]});}
            var Q23;
            {var subQ0=sQuery(id+"F0.wireOp",EDGE,"E11.50.0");Q23=makeQuery(id+"F0.imprint","IMPRINT",FACE,{"disambiguationData":[TD([[makeQuery(id+"F0.imprint","IMPRINT",EDGE,{"derivedFrom":subQ0}),-1.0]])]});}
            var Q24;
            {var subQ0=sQuery(id+"F0.wireOp",EDGE,"E11.34.0");Q24=makeQuery(id+"F0.imprint","IMPRINT",FACE,{"disambiguationData":[TD([[makeQuery(id+"F0.imprint","IMPRINT",EDGE,{"derivedFrom":subQ0}),-1.0]])]});}
            var Q25;
            {var subQ0=sQuery(id+"F0.wireOp",EDGE,"E11.98.0");Q25=makeQuery(id+"F0.imprint","IMPRINT",FACE,{"disambiguationData":[TD([[makeQuery(id+"F0.imprint","IMPRINT",EDGE,{"derivedFrom":subQ0}),-1.0]])]});}
            var Q26;
            {var subQ0=sQuery(id+"F0.wireOp",EDGE,"E11.19.0");Q26=makeQuery(id+"F0.imprint","IMPRINT",FACE,{"disambiguationData":[TD([[makeQuery(id+"F0.imprint","IMPRINT",EDGE,{"derivedFrom":subQ0}),-1.0]])]});}
            var Q27;
            {var subQ0=sQuery(id+"F0.wireOp",EDGE,"E11.83.0");Q27=makeQuery(id+"F0.imprint","IMPRINT",FACE,{"disambiguationData":[TD([[makeQuery(id+"F0.imprint","IMPRINT",EDGE,{"derivedFrom":subQ0}),-1.0]])]});}
            var Q28;
            {var subQ0=sQuery(id+"F0.wireOp",EDGE,"E11.67.0");Q28=makeQuery(id+"F0.imprint","IMPRINT",FACE,{"disambiguationData":[TD([[makeQuery(id+"F0.imprint","IMPRINT",EDGE,{"derivedFrom":subQ0}),-1.0]])]});}
            var Q29;
            {var subQ0=sQuery(id+"F0.wireOp",EDGE,"E11.51.0");Q29=makeQuery(id+"F0.imprint","IMPRINT",FACE,{"disambiguationData":[TD([[makeQuery(id+"F0.imprint","IMPRINT",EDGE,{"derivedFrom":subQ0}),-1.0]])]});}
            var Q30;
            {var subQ0=sQuery(id+"F0.wireOp",EDGE,"E11.35.0");Q30=makeQuery(id+"F0.imprint","IMPRINT",FACE,{"disambiguationData":[TD([[makeQuery(id+"F0.imprint","IMPRINT",EDGE,{"derivedFrom":subQ0}),-1.0]])]});}
            var Q31;
            {var subQ0=sQuery(id+"F0.wireOp",EDGE,"E9.trimOffspring");Q31=makeQuery(id+"F0.imprint","IMPRINT",FACE,{"disambiguationData":[TD([[makeQuery(id+"F0.imprint","IMPRINT",EDGE,{"derivedFrom":subQ0}),-1.0]])]});}
            var Q32;
            {var subQ0=sQuery(id+"F0.wireOp",EDGE,"E11.20.0");Q32=makeQuery(id+"F0.imprint","IMPRINT",FACE,{"disambiguationData":[TD([[makeQuery(id+"F0.imprint","IMPRINT",EDGE,{"derivedFrom":subQ0}),-1.0]])]});}
            var Q33;
            {var subQ0=sQuery(id+"F0.wireOp",EDGE,"E11.84.0");Q33=makeQuery(id+"F0.imprint","IMPRINT",FACE,{"disambiguationData":[TD([[makeQuery(id+"F0.imprint","IMPRINT",EDGE,{"derivedFrom":subQ0}),-1.0]])]});}
            var Q34;
            {var subQ0=sQuery(id+"F0.wireOp",EDGE,"E11.68.0");Q34=makeQuery(id+"F0.imprint","IMPRINT",FACE,{"disambiguationData":[TD([[makeQuery(id+"F0.imprint","IMPRINT",EDGE,{"derivedFrom":subQ0}),-1.0]])]});}
            var Q35;
            {var subQ0=sQuery(id+"F0.wireOp",EDGE,"E11.52.0");Q35=makeQuery(id+"F0.imprint","IMPRINT",FACE,{"disambiguationData":[TD([[makeQuery(id+"F0.imprint","IMPRINT",EDGE,{"derivedFrom":subQ0}),-1.0]])]});}
            var Q36;
            {var subQ0=sQuery(id+"F0.wireOp",EDGE,"E11.36.0");Q36=makeQuery(id+"F0.imprint","IMPRINT",FACE,{"disambiguationData":[TD([[makeQuery(id+"F0.imprint","IMPRINT",EDGE,{"derivedFrom":subQ0}),-1.0]])]});}
            var Q37;
            Q37=makeQuery(id+"F0.imprint","IMPRINT",FACE,{"disambiguationData":[TD([[makeQuery(id+"F0.imprint","IMPRINT",EDGE,{"derivedFrom":sQuery(id+"F0.wireOp",EDGE,"E2.0")}),-1.0]])]});
            var Q38;
            {var subQ0=sQuery(id+"F0.wireOp",EDGE,"E11.21.0");Q38=makeQuery(id+"F0.imprint","IMPRINT",FACE,{"disambiguationData":[TD([[makeQuery(id+"F0.imprint","IMPRINT",EDGE,{"derivedFrom":subQ0}),-1.0]])]});}
            var Q39;
            {var subQ0=sQuery(id+"F0.wireOp",EDGE,"E11.85.0");Q39=makeQuery(id+"F0.imprint","IMPRINT",FACE,{"disambiguationData":[TD([[makeQuery(id+"F0.imprint","IMPRINT",EDGE,{"derivedFrom":subQ0}),-1.0]])]});}
            var Q40;
            {var subQ0=sQuery(id+"F0.wireOp",EDGE,"E11.69.0");Q40=makeQuery(id+"F0.imprint","IMPRINT",FACE,{"disambiguationData":[TD([[makeQuery(id+"F0.imprint","IMPRINT",EDGE,{"derivedFrom":subQ0}),-1.0]])]});}
            var Q41;
            {var subQ0=sQuery(id+"F0.wireOp",EDGE,"E11.53.0");Q41=makeQuery(id+"F0.imprint","IMPRINT",FACE,{"disambiguationData":[TD([[makeQuery(id+"F0.imprint","IMPRINT",EDGE,{"derivedFrom":subQ0}),-1.0]])]});}
            var Q42;
            {var subQ0=sQuery(id+"F0.wireOp",EDGE,"E11.37.0");Q42=makeQuery(id+"F0.imprint","IMPRINT",FACE,{"disambiguationData":[TD([[makeQuery(id+"F0.imprint","IMPRINT",EDGE,{"derivedFrom":subQ0}),-1.0]])]});}
            var Q43;
            Q43=makeQuery(id+"F0.imprint","IMPRINT",FACE,{"disambiguationData":[TD([[makeQuery(id+"F0.imprint","IMPRINT",EDGE,{"derivedFrom":sQuery(id+"F0.wireOp",EDGE,"E3.0")}),-1.0]])]});
            var Q44;
            {var subQ0=sQuery(id+"F0.wireOp",EDGE,"E11.22.0");Q44=makeQuery(id+"F0.imprint","IMPRINT",FACE,{"disambiguationData":[TD([[makeQuery(id+"F0.imprint","IMPRINT",EDGE,{"derivedFrom":subQ0}),-1.0]])]});}
            var Q45;
            {var subQ0=sQuery(id+"F0.wireOp",EDGE,"E11.86.0");Q45=makeQuery(id+"F0.imprint","IMPRINT",FACE,{"disambiguationData":[TD([[makeQuery(id+"F0.imprint","IMPRINT",EDGE,{"derivedFrom":subQ0}),-1.0]])]});}
            var Q46;
            {var subQ0=sQuery(id+"F0.wireOp",EDGE,"E11.70.0");Q46=makeQuery(id+"F0.imprint","IMPRINT",FACE,{"disambiguationData":[TD([[makeQuery(id+"F0.imprint","IMPRINT",EDGE,{"derivedFrom":subQ0}),-1.0]])]});}
            var Q47;
            {var subQ0=sQuery(id+"F0.wireOp",EDGE,"E11.38.0");Q47=makeQuery(id+"F0.imprint","IMPRINT",FACE,{"disambiguationData":[TD([[makeQuery(id+"F0.imprint","IMPRINT",EDGE,{"derivedFrom":subQ0}),-1.0]])]});}
            var Q48;
            Q48=makeQuery(id+"F0.imprint","IMPRINT",FACE,{"disambiguationData":[TD([[makeQuery(id+"F0.imprint","IMPRINT",EDGE,{"derivedFrom":sQuery(id+"F0.wireOp",EDGE,"E4.0")}),-1.0]])]});
            var Q49;
            Q49=makeQuery(id+"F0.imprint","IMPRINT",FACE,{"disambiguationData":[TD([[makeQuery(id+"F0.imprint","IMPRINT",EDGE,{"derivedFrom":sQuery(id+"F0.wireOp",EDGE,"E5.0")}),-1.0]])]});
            var Q50;
            {var subQ0=sQuery(id+"F0.wireOp",EDGE,"E11.87.0");Q50=makeQuery(id+"F0.imprint","IMPRINT",FACE,{"disambiguationData":[TD([[makeQuery(id+"F0.imprint","IMPRINT",EDGE,{"derivedFrom":subQ0}),-1.0]])]});}
            var Q51;
            {var subQ0=sQuery(id+"F0.wireOp",EDGE,"E11.71.0");Q51=makeQuery(id+"F0.imprint","IMPRINT",FACE,{"disambiguationData":[TD([[makeQuery(id+"F0.imprint","IMPRINT",EDGE,{"derivedFrom":subQ0}),-1.0]])]});}
            var Q52;
            {var subQ0=sQuery(id+"F0.wireOp",EDGE,"E11.39.0");Q52=makeQuery(id+"F0.imprint","IMPRINT",FACE,{"disambiguationData":[TD([[makeQuery(id+"F0.imprint","IMPRINT",EDGE,{"derivedFrom":subQ0}),-1.0]])]});}
            var Q53;
            {var subQ0=sQuery(id+"F0.wireOp",EDGE,"E11.23.0");Q53=makeQuery(id+"F0.imprint","IMPRINT",FACE,{"disambiguationData":[TD([[makeQuery(id+"F0.imprint","IMPRINT",EDGE,{"derivedFrom":subQ0}),-1.0]])]});}
            var Q54;
            {var subQ0=sQuery(id+"F0.wireOp",EDGE,"E11.40.0");Q54=makeQuery(id+"F0.imprint","IMPRINT",FACE,{"disambiguationData":[TD([[makeQuery(id+"F0.imprint","IMPRINT",EDGE,{"derivedFrom":subQ0}),-1.0]])]});}
            var Q55;
            {var subQ0=sQuery(id+"F0.wireOp",EDGE,"E11.24.0");Q55=makeQuery(id+"F0.imprint","IMPRINT",FACE,{"disambiguationData":[TD([[makeQuery(id+"F0.imprint","IMPRINT",EDGE,{"derivedFrom":subQ0}),-1.0]])]});}
            var Q56;
            {var subQ0=sQuery(id+"F0.wireOp",EDGE,"E11.88.0");Q56=makeQuery(id+"F0.imprint","IMPRINT",FACE,{"disambiguationData":[TD([[makeQuery(id+"F0.imprint","IMPRINT",EDGE,{"derivedFrom":subQ0}),-1.0]])]});}
            var Q57;
            {var subQ0=sQuery(id+"F0.wireOp",EDGE,"E11.72.0");Q57=makeQuery(id+"F0.imprint","IMPRINT",FACE,{"disambiguationData":[TD([[makeQuery(id+"F0.imprint","IMPRINT",EDGE,{"derivedFrom":subQ0}),-1.0]])]});}
            var Q58;
            {var subQ0=sQuery(id+"F0.wireOp",EDGE,"E11.41.0");Q58=makeQuery(id+"F0.imprint","IMPRINT",FACE,{"disambiguationData":[TD([[makeQuery(id+"F0.imprint","IMPRINT",EDGE,{"derivedFrom":subQ0}),-1.0]])]});}
            var Q59;
            {var subQ0=sQuery(id+"F0.wireOp",EDGE,"E11.25.0");Q59=makeQuery(id+"F0.imprint","IMPRINT",FACE,{"disambiguationData":[TD([[makeQuery(id+"F0.imprint","IMPRINT",EDGE,{"derivedFrom":subQ0}),-1.0]])]});}
            var Q60;
            {var subQ0=sQuery(id+"F0.wireOp",EDGE,"E11.89.0");Q60=makeQuery(id+"F0.imprint","IMPRINT",FACE,{"disambiguationData":[TD([[makeQuery(id+"F0.imprint","IMPRINT",EDGE,{"derivedFrom":subQ0}),-1.0]])]});}
            var Q61;
            {var subQ0=sQuery(id+"F0.wireOp",EDGE,"E11.73.0");Q61=makeQuery(id+"F0.imprint","IMPRINT",FACE,{"disambiguationData":[TD([[makeQuery(id+"F0.imprint","IMPRINT",EDGE,{"derivedFrom":subQ0}),-1.0]])]});}
            var Q62;
            {var subQ0=sQuery(id+"F0.wireOp",EDGE,"E11.42.0");Q62=makeQuery(id+"F0.imprint","IMPRINT",FACE,{"disambiguationData":[TD([[makeQuery(id+"F0.imprint","IMPRINT",EDGE,{"derivedFrom":subQ0}),-1.0]])]});}
            var Q63;
            {var subQ0=sQuery(id+"F0.wireOp",EDGE,"E11.26.0");Q63=makeQuery(id+"F0.imprint","IMPRINT",FACE,{"disambiguationData":[TD([[makeQuery(id+"F0.imprint","IMPRINT",EDGE,{"derivedFrom":subQ0}),-1.0]])]});}
            var Q64;
            {var subQ0=sQuery(id+"F0.wireOp",EDGE,"E11.90.0");Q64=makeQuery(id+"F0.imprint","IMPRINT",FACE,{"disambiguationData":[TD([[makeQuery(id+"F0.imprint","IMPRINT",EDGE,{"derivedFrom":subQ0}),-1.0]])]});}
            var Q65;
            {var subQ0=sQuery(id+"F0.wireOp",EDGE,"E11.74.0");Q65=makeQuery(id+"F0.imprint","IMPRINT",FACE,{"disambiguationData":[TD([[makeQuery(id+"F0.imprint","IMPRINT",EDGE,{"derivedFrom":subQ0}),-1.0]])]});}
            var Q66;
            {var subQ0=sQuery(id+"F0.wireOp",EDGE,"E11.43.0");Q66=makeQuery(id+"F0.imprint","IMPRINT",FACE,{"disambiguationData":[TD([[makeQuery(id+"F0.imprint","IMPRINT",EDGE,{"derivedFrom":subQ0}),-1.0]])]});}
            var Q67;
            {var subQ0=sQuery(id+"F0.wireOp",EDGE,"E11.27.0");Q67=makeQuery(id+"F0.imprint","IMPRINT",FACE,{"disambiguationData":[TD([[makeQuery(id+"F0.imprint","IMPRINT",EDGE,{"derivedFrom":subQ0}),-1.0]])]});}
            var Q68;
            {var subQ0=sQuery(id+"F0.wireOp",EDGE,"E11.91.0");Q68=makeQuery(id+"F0.imprint","IMPRINT",FACE,{"disambiguationData":[TD([[makeQuery(id+"F0.imprint","IMPRINT",EDGE,{"derivedFrom":subQ0}),-1.0]])]});}
            var Q69;
            {var subQ0=sQuery(id+"F0.wireOp",EDGE,"E11.75.0");Q69=makeQuery(id+"F0.imprint","IMPRINT",FACE,{"disambiguationData":[TD([[makeQuery(id+"F0.imprint","IMPRINT",EDGE,{"derivedFrom":subQ0}),-1.0]])]});}
            var Q70;
            {var subQ0=sQuery(id+"F0.wireOp",EDGE,"E11.44.0");Q70=makeQuery(id+"F0.imprint","IMPRINT",FACE,{"disambiguationData":[TD([[makeQuery(id+"F0.imprint","IMPRINT",EDGE,{"derivedFrom":subQ0}),-1.0]])]});}
            var Q71;
            {var subQ0=sQuery(id+"F0.wireOp",EDGE,"E11.28.0");Q71=makeQuery(id+"F0.imprint","IMPRINT",FACE,{"disambiguationData":[TD([[makeQuery(id+"F0.imprint","IMPRINT",EDGE,{"derivedFrom":subQ0}),-1.0]])]});}
            var Q72;
            {var subQ0=sQuery(id+"F0.wireOp",EDGE,"E11.92.0");Q72=makeQuery(id+"F0.imprint","IMPRINT",FACE,{"disambiguationData":[TD([[makeQuery(id+"F0.imprint","IMPRINT",EDGE,{"derivedFrom":subQ0}),-1.0]])]});}
            var Q73;
            {var subQ0=sQuery(id+"F0.wireOp",EDGE,"E11.76.0");Q73=makeQuery(id+"F0.imprint","IMPRINT",FACE,{"disambiguationData":[TD([[makeQuery(id+"F0.imprint","IMPRINT",EDGE,{"derivedFrom":subQ0}),-1.0]])]});}
            var Q74;
            {var subQ0=sQuery(id+"F0.wireOp",EDGE,"E11.45.0");Q74=makeQuery(id+"F0.imprint","IMPRINT",FACE,{"disambiguationData":[TD([[makeQuery(id+"F0.imprint","IMPRINT",EDGE,{"derivedFrom":subQ0}),-1.0]])]});}
            var Q75;
            {var subQ0=sQuery(id+"F0.wireOp",EDGE,"E11.29.0");Q75=makeQuery(id+"F0.imprint","IMPRINT",FACE,{"disambiguationData":[TD([[makeQuery(id+"F0.imprint","IMPRINT",EDGE,{"derivedFrom":subQ0}),-1.0]])]});}
            var Q76;
            {var subQ0=sQuery(id+"F0.wireOp",EDGE,"E11.93.0");Q76=makeQuery(id+"F0.imprint","IMPRINT",FACE,{"disambiguationData":[TD([[makeQuery(id+"F0.imprint","IMPRINT",EDGE,{"derivedFrom":subQ0}),-1.0]])]});}
            var Q77;
            {var subQ0=sQuery(id+"F0.wireOp",EDGE,"E11.77.0");Q77=makeQuery(id+"F0.imprint","IMPRINT",FACE,{"disambiguationData":[TD([[makeQuery(id+"F0.imprint","IMPRINT",EDGE,{"derivedFrom":subQ0}),-1.0]])]});}
            var Q78;
            {var subQ0=sQuery(id+"F0.wireOp",EDGE,"E11.16.0");Q78=makeQuery(id+"F0.imprint","IMPRINT",FACE,{"disambiguationData":[TD([[makeQuery(id+"F0.imprint","IMPRINT",EDGE,{"derivedFrom":subQ0}),-1.0]])]});}
            var Q79;
            {var subQ0=sQuery(id+"F0.wireOp",EDGE,"E11.14.0");Q79=makeQuery(id+"F0.imprint","IMPRINT",FACE,{"disambiguationData":[TD([[makeQuery(id+"F0.imprint","IMPRINT",EDGE,{"derivedFrom":subQ0}),-1.0]])]});}
            var Q80;
            {var subQ0=sQuery(id+"F0.wireOp",EDGE,"E11.15.0");Q80=makeQuery(id+"F0.imprint","IMPRINT",FACE,{"disambiguationData":[TD([[makeQuery(id+"F0.imprint","IMPRINT",EDGE,{"derivedFrom":subQ0}),-1.0]])]});}
            var Q81;
            {var subQ0=sQuery(id+"F0.wireOp",EDGE,"E11.1.0");Q81=makeQuery(id+"F0.imprint","IMPRINT",FACE,{"disambiguationData":[TD([[makeQuery(id+"F0.imprint","IMPRINT",EDGE,{"derivedFrom":subQ0}),-1.0]])]});}
            var Q82;
            {var subQ0=sQuery(id+"F0.wireOp",EDGE,"E11.2.0");Q82=makeQuery(id+"F0.imprint","IMPRINT",FACE,{"disambiguationData":[TD([[makeQuery(id+"F0.imprint","IMPRINT",EDGE,{"derivedFrom":subQ0}),-1.0]])]});}
            var Q83;
            {var subQ0=sQuery(id+"F0.wireOp",EDGE,"E11.3.0");Q83=makeQuery(id+"F0.imprint","IMPRINT",FACE,{"disambiguationData":[TD([[makeQuery(id+"F0.imprint","IMPRINT",EDGE,{"derivedFrom":subQ0}),-1.0]])]});}
            var Q84;
            {var subQ0=sQuery(id+"F0.wireOp",EDGE,"E11.4.0");Q84=makeQuery(id+"F0.imprint","IMPRINT",FACE,{"disambiguationData":[TD([[makeQuery(id+"F0.imprint","IMPRINT",EDGE,{"derivedFrom":subQ0}),-1.0]])]});}
            var Q85;
            {var subQ0=sQuery(id+"F0.wireOp",EDGE,"E11.5.0");Q85=makeQuery(id+"F0.imprint","IMPRINT",FACE,{"disambiguationData":[TD([[makeQuery(id+"F0.imprint","IMPRINT",EDGE,{"derivedFrom":subQ0}),-1.0]])]});}
            var Q86;
            {var subQ0=sQuery(id+"F0.wireOp",EDGE,"E11.6.0");Q86=makeQuery(id+"F0.imprint","IMPRINT",FACE,{"disambiguationData":[TD([[makeQuery(id+"F0.imprint","IMPRINT",EDGE,{"derivedFrom":subQ0}),-1.0]])]});}
            var Q87;
            {var subQ0=sQuery(id+"F0.wireOp",EDGE,"E11.7.0");Q87=makeQuery(id+"F0.imprint","IMPRINT",FACE,{"disambiguationData":[TD([[makeQuery(id+"F0.imprint","IMPRINT",EDGE,{"derivedFrom":subQ0}),-1.0]])]});}
            var Q88;
            {var subQ0=sQuery(id+"F0.wireOp",EDGE,"E11.8.0");Q88=makeQuery(id+"F0.imprint","IMPRINT",FACE,{"disambiguationData":[TD([[makeQuery(id+"F0.imprint","IMPRINT",EDGE,{"derivedFrom":subQ0}),-1.0]])]});}
            var Q89;
            {var subQ0=sQuery(id+"F0.wireOp",EDGE,"E11.9.0");Q89=makeQuery(id+"F0.imprint","IMPRINT",FACE,{"disambiguationData":[TD([[makeQuery(id+"F0.imprint","IMPRINT",EDGE,{"derivedFrom":subQ0}),-1.0]])]});}
            var Q90;
            {var subQ0=sQuery(id+"F0.wireOp",EDGE,"E11.10.0");Q90=makeQuery(id+"F0.imprint","IMPRINT",FACE,{"disambiguationData":[TD([[makeQuery(id+"F0.imprint","IMPRINT",EDGE,{"derivedFrom":subQ0}),-1.0]])]});}
            var Q91;
            {var subQ0=sQuery(id+"F0.wireOp",EDGE,"E11.11.0");Q91=makeQuery(id+"F0.imprint","IMPRINT",FACE,{"disambiguationData":[TD([[makeQuery(id+"F0.imprint","IMPRINT",EDGE,{"derivedFrom":subQ0}),-1.0]])]});}
            var Q92;
            {var subQ0=sQuery(id+"F0.wireOp",EDGE,"E11.12.0");Q92=makeQuery(id+"F0.imprint","IMPRINT",FACE,{"disambiguationData":[TD([[makeQuery(id+"F0.imprint","IMPRINT",EDGE,{"derivedFrom":subQ0}),-1.0]])]});}
            var Q93;
            {var subQ0=sQuery(id+"F0.wireOp",EDGE,"E11.13.0");Q93=makeQuery(id+"F0.imprint","IMPRINT",FACE,{"disambiguationData":[TD([[makeQuery(id+"F0.imprint","IMPRINT",EDGE,{"derivedFrom":subQ0}),-1.0]])]});}
            var Q94;
            {var subQ0=sQuery(id+"F0.wireOp",EDGE,"E11.62.0");Q94=makeQuery(id+"F0.imprint","IMPRINT",FACE,{"disambiguationData":[TD([[makeQuery(id+"F0.imprint","IMPRINT",EDGE,{"derivedFrom":subQ0}),-1.0]])]});}
            var Q95;
            {var subQ0=sQuery(id+"F0.wireOp",EDGE,"E11.54.0");Q95=makeQuery(id+"F0.imprint","IMPRINT",FACE,{"disambiguationData":[TD([[makeQuery(id+"F0.imprint","IMPRINT",EDGE,{"derivedFrom":subQ0}),-1.0]])]});}
            var Q96;
            {var subQ0=sQuery(id+"F0.wireOp",EDGE,"E11.55.0");Q96=makeQuery(id+"F0.imprint","IMPRINT",FACE,{"disambiguationData":[TD([[makeQuery(id+"F0.imprint","IMPRINT",EDGE,{"derivedFrom":subQ0}),-1.0]])]});}
            var Q97;
            {var subQ0=sQuery(id+"F0.wireOp",EDGE,"E11.56.0");Q97=makeQuery(id+"F0.imprint","IMPRINT",FACE,{"disambiguationData":[TD([[makeQuery(id+"F0.imprint","IMPRINT",EDGE,{"derivedFrom":subQ0}),-1.0]])]});}
            var Q98;
            {var subQ0=sQuery(id+"F0.wireOp",EDGE,"E11.57.0");Q98=makeQuery(id+"F0.imprint","IMPRINT",FACE,{"disambiguationData":[TD([[makeQuery(id+"F0.imprint","IMPRINT",EDGE,{"derivedFrom":subQ0}),-1.0]])]});}
            var Q99;
            {var subQ0=sQuery(id+"F0.wireOp",EDGE,"E11.58.0");Q99=makeQuery(id+"F0.imprint","IMPRINT",FACE,{"disambiguationData":[TD([[makeQuery(id+"F0.imprint","IMPRINT",EDGE,{"derivedFrom":subQ0}),-1.0]])]});}
            var Q100;
            {var subQ0=sQuery(id+"F0.wireOp",EDGE,"E11.59.0");Q100=makeQuery(id+"F0.imprint","IMPRINT",FACE,{"disambiguationData":[TD([[makeQuery(id+"F0.imprint","IMPRINT",EDGE,{"derivedFrom":subQ0}),-1.0]])]});}
            var Q101;
            {var subQ0=sQuery(id+"F0.wireOp",EDGE,"E11.60.0");Q101=makeQuery(id+"F0.imprint","IMPRINT",FACE,{"disambiguationData":[TD([[makeQuery(id+"F0.imprint","IMPRINT",EDGE,{"derivedFrom":subQ0}),-1.0]])]});}
            var Q102;
            {var subQ0=sQuery(id+"F0.wireOp",EDGE,"E11.61.0");Q102=makeQuery(id+"F0.imprint","IMPRINT",FACE,{"disambiguationData":[TD([[makeQuery(id+"F0.imprint","IMPRINT",EDGE,{"derivedFrom":subQ0}),-1.0]])]});}
            var Q103;
            Q103=makeQuery(id+"F0.imprint","IMPRINT",FACE,{"disambiguationData":[TD([[makeQuery(id+"F0.imprint","IMPRINT",EDGE,{"derivedFrom":sQuery(id+"F0.wireOp",EDGE,"E2.0")}),1.0]])]});
            extrude(context, id + "F1", {"entities" : qUnion([Q0, Q1, Q2, Q3, Q4, Q5, Q6, Q7, Q8, Q9, Q10, Q11, Q12, Q13, Q14, Q15, Q16, Q17, Q18, Q19, Q20, Q21, Q22, Q23, Q24, Q25, Q26, Q27, Q28, Q29, Q30, Q31, Q32, Q33, Q34, Q35, Q36, Q37, Q38, Q39, Q40, Q41, Q42, Q43, Q44, Q45, Q46, Q47, Q48, Q49, Q50, Q51, Q52, Q53, Q54, Q55, Q56, Q57, Q58, Q59, Q60, Q61, Q62, Q63, Q64, Q65, Q66, Q67, Q68, Q69, Q70, Q71, Q72, Q73, Q74, Q75, Q76, Q77, Q78, Q79, Q80, Q81, Q82, Q83, Q84, Q85, Q86, Q87, Q88, Q89, Q90, Q91, Q92, Q93, Q94, Q95, Q96, Q97, Q98, Q99, Q100, Q101, Q102, Q103]), "depth" : 5.5 * mm});
        }
    });
